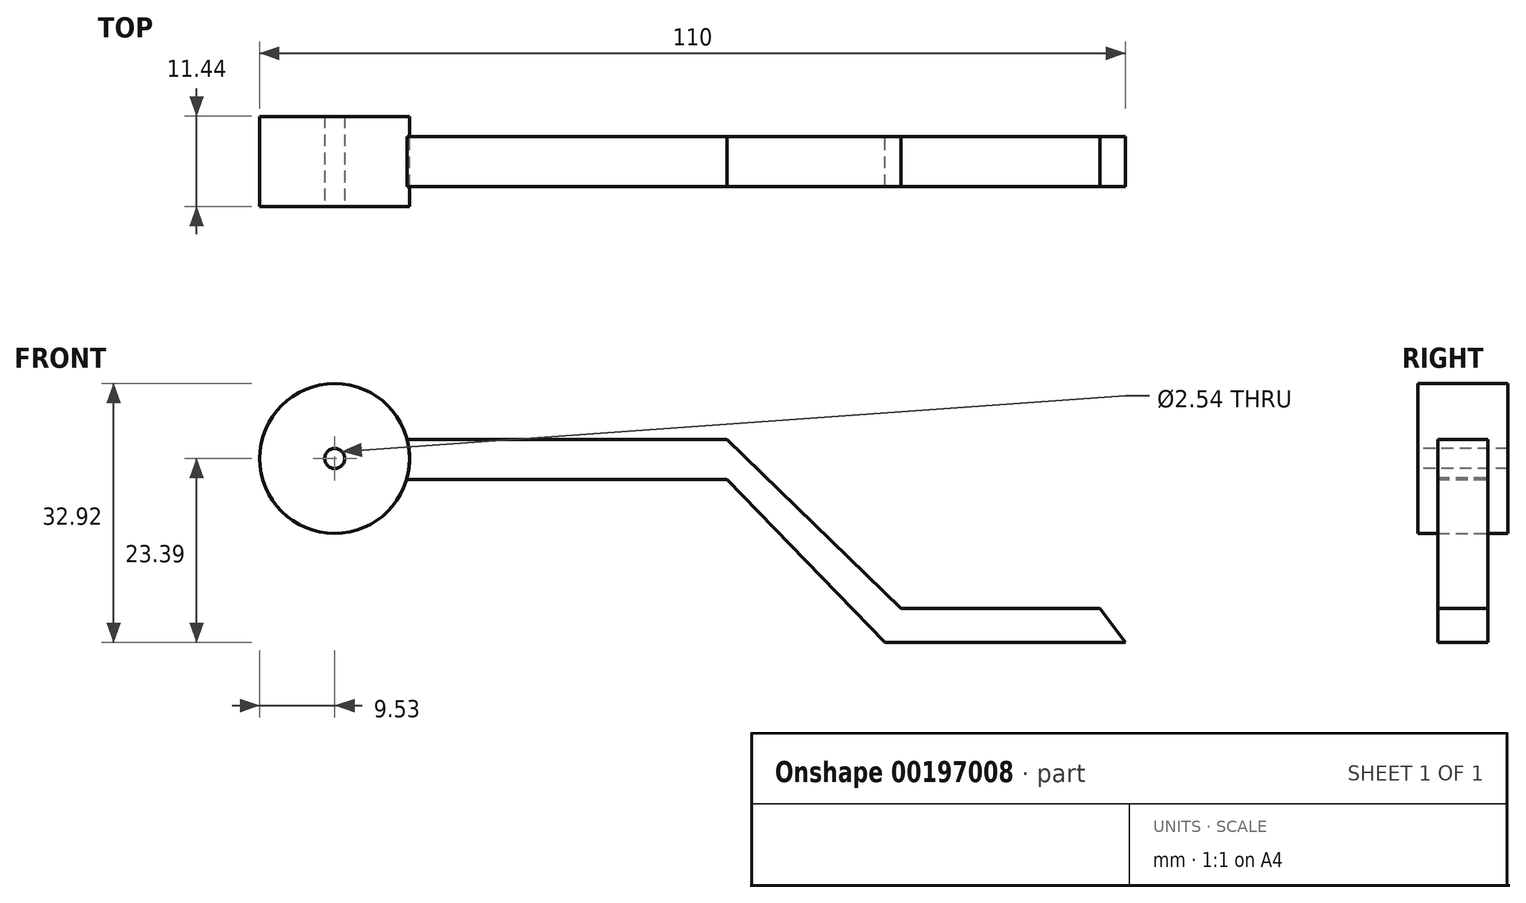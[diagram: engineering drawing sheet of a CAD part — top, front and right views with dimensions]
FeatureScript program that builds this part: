
annotation { "Feature Type Name" : "Feature", "Feature Type Description" : "" }
export const myFeature = defineFeature(function(context is Context, id is Id, definition is map)
    precondition{}
    {
        {
            var Q0;
            Q0=qCreatedBy(makeId("Front.planeOp"),FACE);
            var sketch = newSketch(context, id + "F0", { "sketchPlane" : qUnion([Q0])});
            skCircle(sketch, "E0", {"center": v(0, 0) * mm, "radius": 9.53 * mm});
            skLineSegment(sketch, "E1.bottom", {"start": v(9.22, 2.4) * mm, "end": v(49.86, 2.4) * mm});
            skLineSegment(sketch, "E1.top", {"start": v(9.22, -2.69) * mm, "end": v(49.86, -2.69) * mm});
            skLineSegment(sketch, "E1.left", {"start": v(9.22, 2.4) * mm, "end": v(9.22, -2.69) * mm});
            skLineSegment(sketch, "E1.right", {"start": v(49.86, 2.4) * mm, "end": v(49.86, -2.69) * mm});
            skLineSegment(sketch, "E2", {"start": v(49.86, -2.69) * mm, "end": v(69.9, -23.4) * mm});
            skLineSegment(sketch, "E3", {"start": v(100.47, -23.4) * mm, "end": v(97.2, -19.02) * mm});
            skLineSegment(sketch, "E4", {"start": v(49.86, 2.4) * mm, "end": v(71.9, -19.02) * mm});
            skLineSegment(sketch, "E5", {"start": v(71.9, -19.02) * mm, "end": v(97.2, -19.02) * mm});
            skLineSegment(sketch, "E6", {"start": v(100.47, -23.4) * mm, "end": v(69.9, -23.4) * mm});
            skSolve(sketch);
        }
        {
            var Q0;
            {var subQ0=sQuery(id+"F0.wireOp",EDGE,"E1.left");var subQ1=sQuery(id+"F0.wireOp",EDGE,"E0");var subQ3=makeQuery(id+"F0.imprint","INTERSECT",VERTEX,{"derivedFrom":[subQ1,subQ0]});Q0=makeQuery(id+"F0.imprint","IMPRINT",FACE,{"disambiguationData":[TD([[makeQuery(id+"F0.imprint","IMPRINT",EDGE,{"disambiguationData":[TD([[subQ3,1.0]])],"derivedFrom":subQ1}),1.0]])]});}
            var Q1;
            {var subQ0=sQuery(id+"F0.wireOp",EDGE,"E1.left");var subQ1=sQuery(id+"F0.wireOp",EDGE,"E0");var subQ3=makeQuery(id+"F0.imprint","INTERSECT",VERTEX,{"derivedFrom":[subQ1,subQ0]});Q1=makeQuery(id+"F0.imprint","IMPRINT",FACE,{"disambiguationData":[TD([[makeQuery(id+"F0.imprint","IMPRINT",EDGE,{"disambiguationData":[TD([[subQ3,-1.0]])],"derivedFrom":subQ1}),1.0]])]});}
            extrude(context, id + "F1", {"entities" : qUnion([Q0, Q1]), "endBound" : BoundingType.SYMMETRIC, "depth" : 11.43 * mm});
        }
        {
            var Q0;
            {var subQ4=sQuery(id+"F0.wireOp",EDGE,"E1.bottom");Q0=makeQuery(id+"F0.imprint","IMPRINT",FACE,{"disambiguationData":[TD([[makeQuery(id+"F0.imprint","IMPRINT",EDGE,{"derivedFrom":subQ4}),-1.0]])]});}
            var Q1;
            Q1=makeQuery(id+"F0.imprint","IMPRINT",FACE,{"disambiguationData":[TD([[makeQuery(id+"F0.imprint","IMPRINT",EDGE,{"derivedFrom":sQuery(id+"F0.wireOp",EDGE,"E1.right")}),1.0]])]});
            extrude(context, id + "F2", {"entities" : qUnion([Q0, Q1]), "endBound" : BoundingType.SYMMETRIC, "depth" : 6.35 * mm});
        }
        {
            var Q0;
            Q0=makeQuery(id+"F1.opExtrude","CAP_FACE",FACE,{"disambiguationData":[OSD([sQuery(id+"F0.wireOp",EDGE,"E0")])],"isStart":false});
            var sketch = newSketch(context, id + "F3", { "sketchPlane" : qUnion([Q0])});
            skCircle(sketch, "E7", {"center": v(0, 0) * mm, "radius": 1.27 * mm});
            skSolve(sketch);
        }
        {
            var Q0;
            Q0=makeQuery(id+"F3.imprint","IMPRINT",FACE,{"disambiguationData":[TD([[makeQuery(id+"F3.imprint","IMPRINT",EDGE,{"derivedFrom":sQuery(id+"F3.wireOp",EDGE,"E7")}),1.0]])]});
            extrude(context, id + "F4", {"entities" : qUnion([Q0]), "operationType" : NewBodyOperationType.REMOVE, "oppositeDirection" : true, "depth" : 25.4 * mm});
        }
    });
